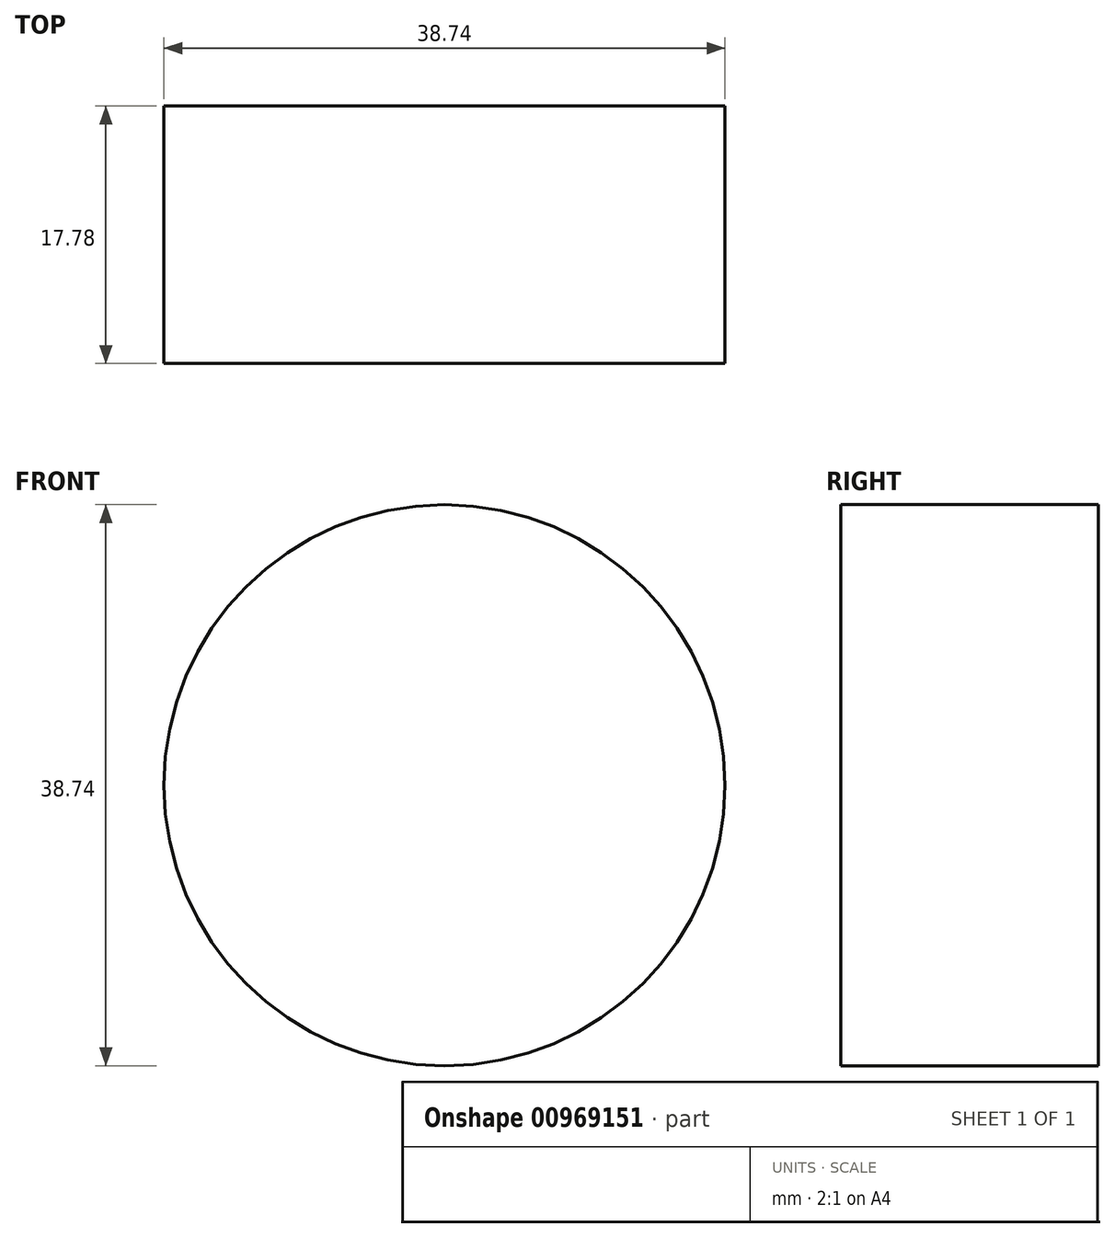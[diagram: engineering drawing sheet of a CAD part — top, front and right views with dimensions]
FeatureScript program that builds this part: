
annotation { "Feature Type Name" : "Feature", "Feature Type Description" : "" }
export const myFeature = defineFeature(function(context is Context, id is Id, definition is map)
    precondition{}
    {
        {
            var Q0;
            Q0=qCreatedBy(makeId("Front.planeOp"),FACE);
            var sketch = newSketch(context, id + "F0", { "sketchPlane" : qUnion([Q0])});
            skCircle(sketch, "E0", {"center": v(0, 0) * mm, "radius": 75.82 * mm});
            skSolve(sketch);
        }
        {
            var Q0;
            Q0=makeQuery(id+"F0.imprint","IMPRINT",FACE,{"disambiguationData":[TD([[makeQuery(id+"F0.imprint","IMPRINT",EDGE,{"derivedFrom":sQuery(id+"F0.wireOp",EDGE,"E0")}),1.0]])]});
            var Q1;
            Q1=sQuery(id+"F0.wireOp",EDGE,"E0");
            extrude(context, id + "F1", {"entities" : qUnion([Q0]), "bodyType" : ToolBodyType.SURFACE, "surfaceEntities" : qUnion([Q1]), "endBound" : BoundingType.SYMMETRIC, "depth" : 38.1 * mm, "offsetDistance" : 25.4 * mm});
        }
        {
            var Q0;
            Q0 = qSketchRegion(id + "F0", true);
            var sketch = newSketch(context, id + "F2", { "sketchPlane" : qUnion([Q0])});
            skCircle(sketch, "E1", {"center": v(0, 0) * mm, "radius": 19.37 * mm});
            skSolve(sketch);
        }
        {
            var Q0;
            Q0=sQuery(id+"F2.wireOp",EDGE,"E1");
            extrude(context, id + "F3", {"bodyType" : ToolBodyType.SURFACE, "surfaceEntities" : qUnion([Q0]), "endBound" : BoundingType.SYMMETRIC, "depth" : 17.78 * mm, "offsetDistance" : 25.4 * mm});
        }
        {
            var Q0;
            Q0=makeQuery(id+"F2.imprint","IMPRINT",FACE,{"disambiguationData":[TD([[makeQuery(id+"F2.imprint","IMPRINT",EDGE,{"derivedFrom":sQuery(id+"F2.wireOp",EDGE,"E1")}),1.0]])]});
            extrude(context, id + "F4", {"entities" : qUnion([Q0]), "endBound" : BoundingType.SYMMETRIC, "depth" : 17.78 * mm, "offsetDistance" : 25.4 * mm});
        }
    });
